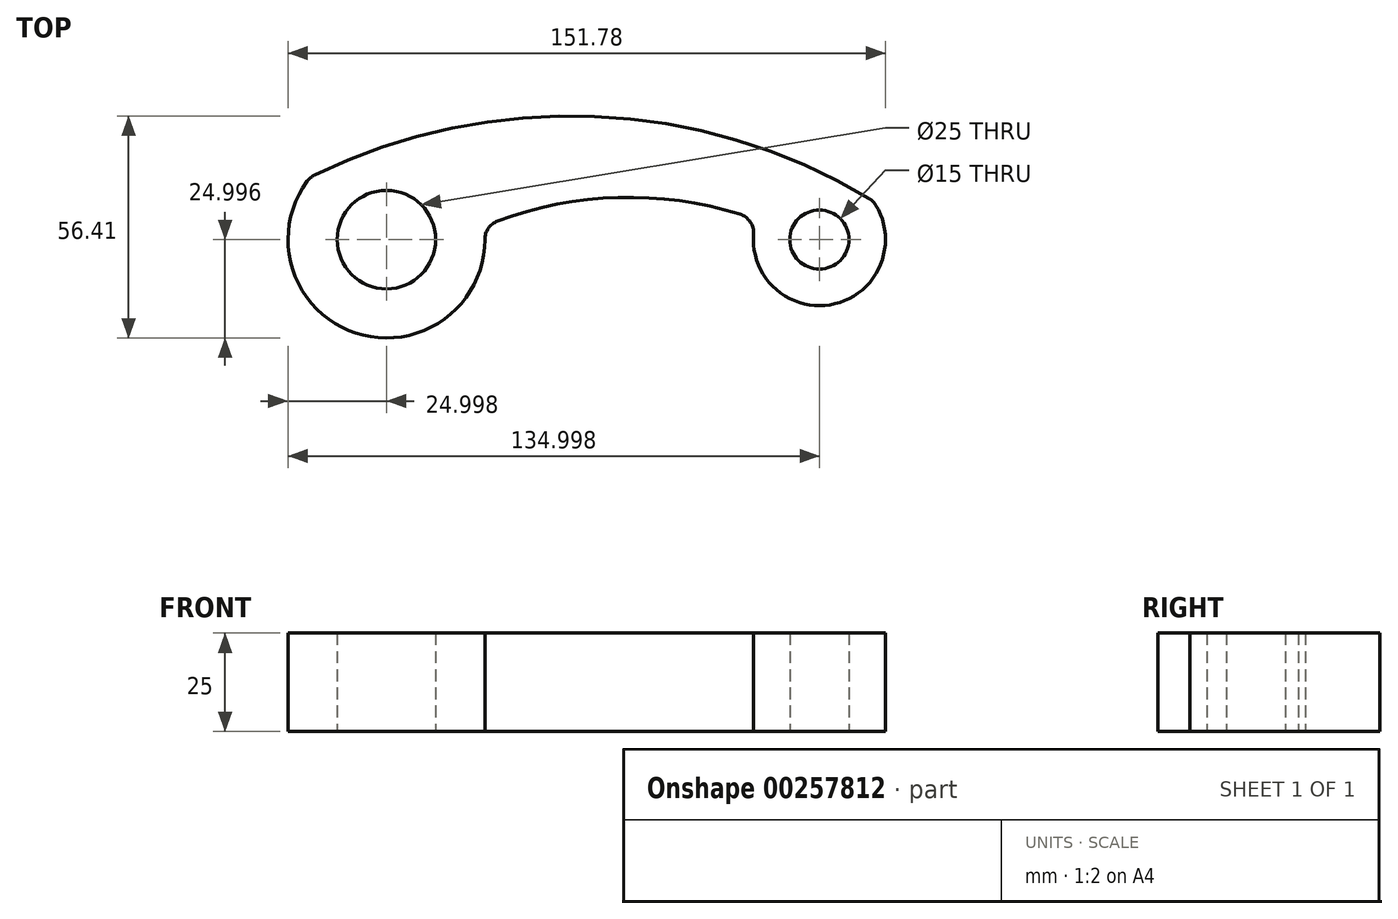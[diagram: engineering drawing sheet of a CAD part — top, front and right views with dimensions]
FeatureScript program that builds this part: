
annotation { "Feature Type Name" : "Feature", "Feature Type Description" : "" }
export const myFeature = defineFeature(function(context is Context, id is Id, definition is map)
    precondition{}
    {
        {
            var Q0;
            Q0=qCreatedBy(makeId("Top.planeOp"),FACE);
            var sketch = newSketch(context, id + "F0", { "sketchPlane" : qUnion([Q0])});
            skCircle(sketch, "E0", {"center": v(-56.9, 34.17) * mm, "radius": 12.5 * mm});
            skCircle(sketch, "E1", {"center": v(53.1, 34.17) * mm, "radius": 7.5 * mm});
            skArc(sketch, "E2", {"start": v(-77.03, 48.99) * mm, "mid": v(-64.7, 10.41) * mm, "end": v(-31.9, 34.19) * mm});
            skArc(sketch, "E3", {"start": v(36.37, 35.47) * mm, "mid": v(57.04, 17.86) * mm, "end": v(67.38, 42.97) * mm});
            skLineSegment(sketch, "E4", {"start": v(-55.33, -50.09) * mm, "end": v(4.67, -50.09) * mm});
            skArc(sketch, "E5", {"start": v(32.87, 40.63) * mm, "mid": v(1.96, 44.87) * mm, "end": v(-28.66, 38.87) * mm});
            skLineSegment(sketch, "E6.trimOffspring", {"start": v(-56.9, 9.17) * mm, "end": v(-55.33, -50.09) * mm});
            skArc(sketch, "E7", {"start": v(65.7, 44.64) * mm, "mid": v(-4.01, 65.45) * mm, "end": v(-75.2, 50.51) * mm});
            skPoint(sketch, "E7.first.point", {"position": v(-76.25, 50) * mm});
            skPoint(sketch, "E7.second.point", {"position": v(66.65, 44.06) * mm});
            skPoint(sketch, "E7.third.point", {"position": v(33.01, 59.14) * mm});
            skArc(sketch, "E8.filletArc", {"start": v(-75.2, 50.51) * mm, "mid": v(-76.21, 49.86) * mm, "end": v(-77.03, 48.99) * mm});
            skArc(sketch, "E9.filletArc", {"start": v(67.38, 42.97) * mm, "mid": v(66.64, 43.9) * mm, "end": v(65.7, 44.64) * mm});
            skPoint(sketch, "E10.visualSharp", {"position": v(37.1, 39.2) * mm});
            skArc(sketch, "E10.filletArc", {"start": v(36.37, 35.47) * mm, "mid": v(35.52, 38.66) * mm, "end": v(32.87, 40.63) * mm});
            skPoint(sketch, "E11.visualSharp", {"position": v(-32.12, 37.5) * mm});
            skArc(sketch, "E11.filletArc", {"start": v(-28.66, 38.87) * mm, "mid": v(-31.01, 37.04) * mm, "end": v(-31.9, 34.19) * mm});
            skSolve(sketch);
        }
        {
            var Q0;
            Q0=makeQuery(id+"F0.imprint","IMPRINT",FACE,{"disambiguationData":[TD([[makeQuery(id+"F0.imprint","IMPRINT",EDGE,{"derivedFrom":sQuery(id+"F0.wireOp",EDGE,"E0")}),-1.0]])]});
            extrude(context, id + "F1", {"entities" : qUnion([Q0]), "depth" : 25 * mm});
        }
    });
